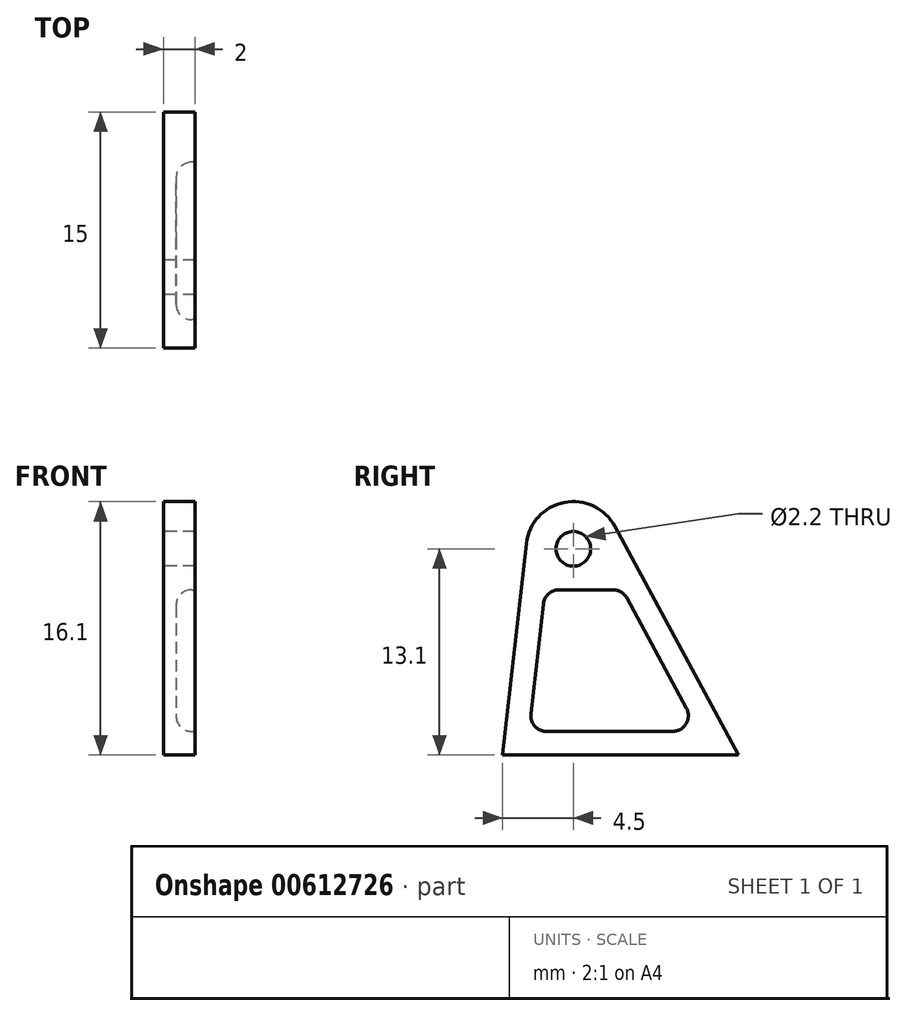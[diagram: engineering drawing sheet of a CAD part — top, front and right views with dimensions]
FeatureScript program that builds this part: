
annotation { "Feature Type Name" : "Feature", "Feature Type Description" : "" }
export const myFeature = defineFeature(function(context is Context, id is Id, definition is map)
    precondition{}
    {
        {
            var Q0;
            Q0=qCreatedBy(makeId("Right.planeOp"),FACE);
            var sketch = newSketch(context, id + "F0", { "sketchPlane" : qUnion([Q0])});
            skCircle(sketch, "E0", {"center": v(0, 13.1) * mm, "radius": 1.1 * mm});
            skLineSegment(sketch, "E1", {"start": v(10.5, 0) * mm, "end": v(2.64, 14.53) * mm});
            skLineSegment(sketch, "E2", {"start": v(10.5, 0) * mm, "end": v(-4.5, 0) * mm});
            skLineSegment(sketch, "E3", {"start": v(-4.5, 0) * mm, "end": v(-2.98, 13.44) * mm});
            skArc(sketch, "E4", {"start": v(2.64, 14.53) * mm, "mid": v(-0.57, 16.05) * mm, "end": v(-2.98, 13.44) * mm});
            skSolve(sketch);
        }
        {
            var Q0;
            Q0=qSketchRegion(id+"F0",true);
            extrude(context, id + "F1", {"entities" : qUnion([Q0]), "depth" : 2 * mm, "offsetDistance" : 25 * mm});
        }
        {
            var Q0;
            Q0=makeQuery(id+"F1.opExtrude","CAP_FACE",FACE,{"disambiguationData":[OSD([sQuery(id+"F0.wireOp",EDGE,"E0"),sQuery(id+"F0.wireOp",EDGE,"E1"),sQuery(id+"F0.wireOp",EDGE,"E2"),sQuery(id+"F0.wireOp",EDGE,"E3"),sQuery(id+"F0.wireOp",EDGE,"E4")])],"isStart":false});
            var sketch = newSketch(context, id + "F2", { "sketchPlane" : qUnion([Q0])});
            skLineSegment(sketch, "E5", {"start": v(-2.82, 1.5) * mm, "end": v(7.98, 1.5) * mm});
            skLineSegment(sketch, "E6", {"start": v(7.98, 1.5) * mm, "end": v(3.11, 10.5) * mm});
            skLineSegment(sketch, "E7", {"start": v(3.11, 10.5) * mm, "end": v(-1.8, 10.5) * mm});
            skLineSegment(sketch, "E8", {"start": v(-1.8, 10.5) * mm, "end": v(-2.82, 1.5) * mm});
            skSolve(sketch);
        }
        {
            var Q0;
            Q0=qSketchRegion(id+"F2",true);
            extrude(context, id + "F3", {"entities" : qUnion([Q0]), "operationType" : NewBodyOperationType.REMOVE, "oppositeDirection" : true, "depth" : 1.2 * mm, "offsetDistance" : 25 * mm});
        }
        {
            var Q0;
            Q0=makeQuery(id+"F3.boolean.opBoolean","COPY",EDGE,{"derivedFrom":makeQuery(id+"F3.opExtrude","SWEPT_EDGE",EDGE,{"disambiguationData":[OSD([sQuery(id+"F2.wireOp",EDGE,"E7"),sQuery(id+"F2.wireOp",EDGE,"E8")])]})});
            var Q1;
            Q1=makeQuery(id+"F3.boolean.opBoolean","COPY",EDGE,{"derivedFrom":makeQuery(id+"F3.opExtrude","SWEPT_EDGE",EDGE,{"disambiguationData":[OSD([sQuery(id+"F2.wireOp",EDGE,"E6"),sQuery(id+"F2.wireOp",EDGE,"E7")])]})});
            var Q2;
            Q2=makeQuery(id+"F3.boolean.opBoolean","COPY",EDGE,{"derivedFrom":makeQuery(id+"F3.opExtrude","SWEPT_EDGE",EDGE,{"disambiguationData":[OSD([sQuery(id+"F2.wireOp",EDGE,"E5"),sQuery(id+"F2.wireOp",EDGE,"E6")])]})});
            var Q3;
            Q3=makeQuery(id+"F3.boolean.opBoolean","COPY",EDGE,{"derivedFrom":makeQuery(id+"F3.opExtrude","SWEPT_EDGE",EDGE,{"disambiguationData":[OSD([sQuery(id+"F2.wireOp",EDGE,"E5"),sQuery(id+"F2.wireOp",EDGE,"E8")])]})});
            fillet(context, id + "F4", {"entities" : qUnion([Q0, Q1, Q2, Q3]), "radius" : 1 * mm, "tangentPropagation" : true, "allowEdgeOverflow" : false});
        }
        {
            var Q0;
            Q0=makeQuery(id+"F3.boolean.opBoolean","COPY",FACE,{"derivedFrom":makeQuery(id+"F3.opExtrude","CAP_FACE",FACE,{"disambiguationData":[OSD([sQuery(id+"F2.wireOp",EDGE,"E5"),sQuery(id+"F2.wireOp",EDGE,"E6"),sQuery(id+"F2.wireOp",EDGE,"E7"),sQuery(id+"F2.wireOp",EDGE,"E8")])],"isStart":false})});
            fillet(context, id + "F5", {"entities" : qUnion([Q0]), "radius" : 1 * mm, "tangentPropagation" : true, "allowEdgeOverflow" : false});
        }
    });
